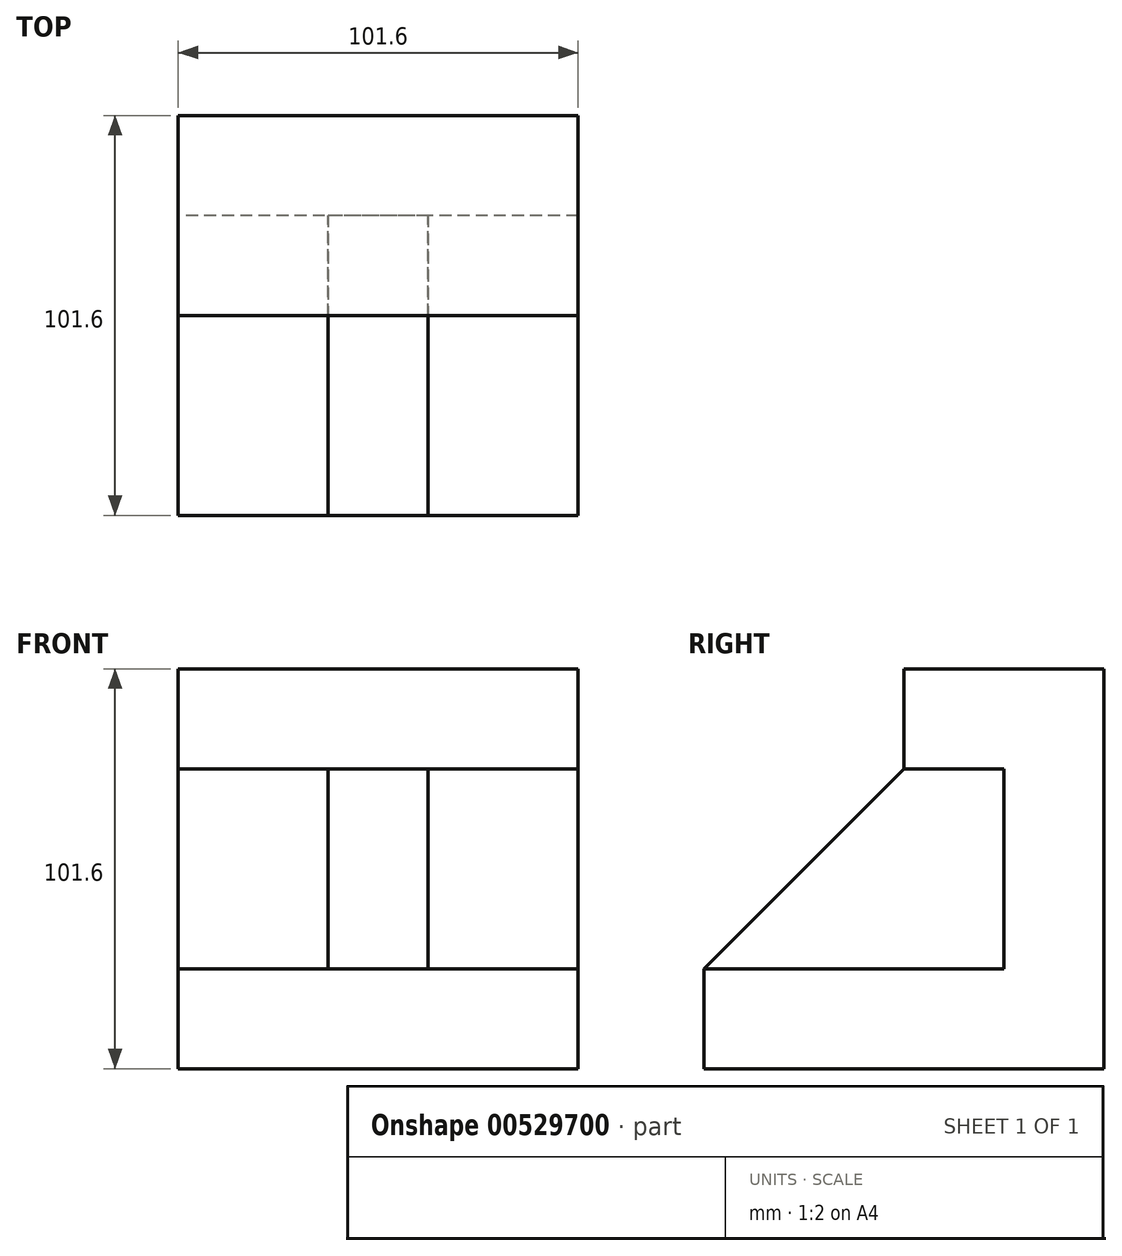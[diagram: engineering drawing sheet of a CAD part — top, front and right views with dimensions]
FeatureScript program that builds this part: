
annotation { "Feature Type Name" : "Feature", "Feature Type Description" : "" }
export const myFeature = defineFeature(function(context is Context, id is Id, definition is map)
    precondition{}
    {
        {
            var Q0;
            Q0=qCreatedBy(makeId("Right.planeOp"),FACE);
            var sketch = newSketch(context, id + "F0", { "sketchPlane" : qUnion([Q0])});
            skLineSegment(sketch, "E0", {"start": v(0, -25.4) * mm, "end": v(-50.8, -25.4) * mm});
            skLineSegment(sketch, "E1", {"start": v(-50.8, -25.4) * mm, "end": v(-50.8, -50.8) * mm});
            skLineSegment(sketch, "E2", {"start": v(-50.8, -50.8) * mm, "end": v(50.8, -50.8) * mm});
            skLineSegment(sketch, "E3", {"start": v(50.8, -50.8) * mm, "end": v(50.8, 50.8) * mm});
            skLineSegment(sketch, "E4", {"start": v(50.8, 50.8) * mm, "end": v(0, 50.8) * mm});
            skLineSegment(sketch, "E5", {"start": v(0, 50.8) * mm, "end": v(0, 25.4) * mm});
            skLineSegment(sketch, "E6", {"start": v(0, 25.4) * mm, "end": v(25.4, 25.4) * mm});
            skLineSegment(sketch, "E7", {"start": v(25.4, 25.4) * mm, "end": v(25.4, -25.4) * mm});
            skLineSegment(sketch, "E8", {"start": v(25.4, -25.4) * mm, "end": v(0, -25.4) * mm});
            skSolve(sketch);
        }
        {
            var Q0;
            Q0=makeQuery(id+"F0.imprint","IMPRINT",FACE,{"disambiguationData":[TD([[makeQuery(id+"F0.imprint","IMPRINT",EDGE,{"derivedFrom":sQuery(id+"F0.wireOp",EDGE,"E0")}),1.0]])]});
            extrude(context, id + "F1", {"entities" : qUnion([Q0]), "depth" : 101.6 * mm, "offsetDistance" : 25.4 * mm});
        }
        {
            var Q0;
            Q0=makeQuery(id+"F1.opExtrude","CAP_FACE",FACE,{"disambiguationData":[OSD([sQuery(id+"F0.wireOp",EDGE,"E0"),sQuery(id+"F0.wireOp",EDGE,"E1"),sQuery(id+"F0.wireOp",EDGE,"E2"),sQuery(id+"F0.wireOp",EDGE,"E3"),sQuery(id+"F0.wireOp",EDGE,"E4"),sQuery(id+"F0.wireOp",EDGE,"E5"),sQuery(id+"F0.wireOp",EDGE,"E6"),sQuery(id+"F0.wireOp",EDGE,"E7"),sQuery(id+"F0.wireOp",EDGE,"E8")])],"isStart":true});
            var sketch = newSketch(context, id + "F2", { "sketchPlane" : qUnion([Q0])});
            skLineSegment(sketch, "E9", {"start": v(-25.4, 25.4) * mm, "end": v(0, 25.4) * mm});
            skLineSegment(sketch, "E10", {"start": v(0, 25.4) * mm, "end": v(50.8, -25.4) * mm});
            skLineSegment(sketch, "E11", {"start": v(50.8, -25.4) * mm, "end": v(-25.4, -25.4) * mm});
            skLineSegment(sketch, "E12", {"start": v(-25.4, -25.4) * mm, "end": v(-25.4, 25.4) * mm});
            skSolve(sketch);
        }
        {
            var Q0;
            Q0=makeQuery(id+"F2.imprint","IMPRINT",FACE,{"disambiguationData":[TD([[makeQuery(id+"F2.imprint","IMPRINT",EDGE,{"derivedFrom":sQuery(id+"F2.wireOp",EDGE,"E9")}),1.0]])]});
            extrude(context, id + "F3", {"entities" : qUnion([Q0]), "oppositeDirection" : true, "depth" : 25.4 * mm, "offsetDistance" : 25.4 * mm});
        }
        {
            var Q0;
            Q0=makeQuery(id+"F3.opExtrude","SWEPT_BODY",BODY,{"disambiguationData":[OSD([sQuery(id+"F2.wireOp",EDGE,"E9"),sQuery(id+"F2.wireOp",EDGE,"E10"),sQuery(id+"F2.wireOp",EDGE,"E11"),sQuery(id+"F2.wireOp",EDGE,"E12")])]});
            transform(context, id + "F4", {"entities" : qUnion([Q0]), "transformType" : TransformType.TRANSLATION_3D, "dx" : 38.1 * mm, "dy" : 0 * mm, "dz" : 0 * mm, "makeCopy" : false});
        }
    });
